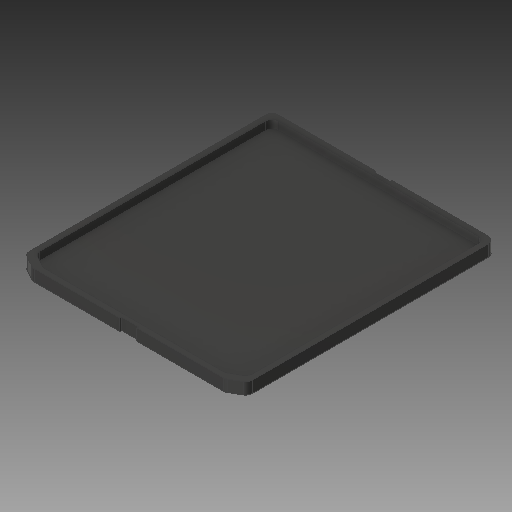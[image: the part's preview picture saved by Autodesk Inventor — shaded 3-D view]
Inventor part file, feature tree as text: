
AUTODESK INVENTOR PART (.ipt)
format: ipt  version: 2019.2 (Build 232265000, 265)  size: 1,129,472 bytes
history: native  units: mm
features: other x9, extrude x4, sketch x2, emboss x1, projected_geometry x1
ambient origin geometry x8: Origin, YZ Plane, XZ Plane, XY Plane, X Axis, Y Axis, Z Axis, Center Point
bodies: Solid3 (feature_tree), Solid2 (feature_tree)
feature tree (17):
  other  "Housing Box 1.ipt"
  sketch  "Sketch3"  dims[d18=10.0mm d19=1.95mm d20=0.0mm]
  extrude  "Extrusion4"  Depth=10.0mm TaperAngle=0.0deg
  extrude  "Extrusion5"  Depth=0.1mm
  extrude  "Extrusion6"  Depth=0.1mm
  extrude  "Extrusion7"  Depth=0.1mm
  emboss  "Emboss1"
  other  "Solid2::Housing Box 1.ipt"
  other  "TaggingFeature1"
  other  "MOTOR1_3"
  other  "MOTOR1_2"
  other  "MOTOR1_1"
  other  "MOTOR2_3"
  other  "MOTOR2_2"
  other  "MOTOR2_1"
  projected_geometry  "Projected Loop1"
  sketch  "Sketch4"  dims[d21=4.9mm d22=0.0mm d23=250.0mm d24=62.565836mm d25=62.565836mm d26=10.0mm d27=1.0mm d28=10.0mm d29=1.0mm d30=10.0mm d31=0.0mm d32=10.0mm d33=0.0mm d34=180.0mm d35=0.1mm d36=0.0mm]
